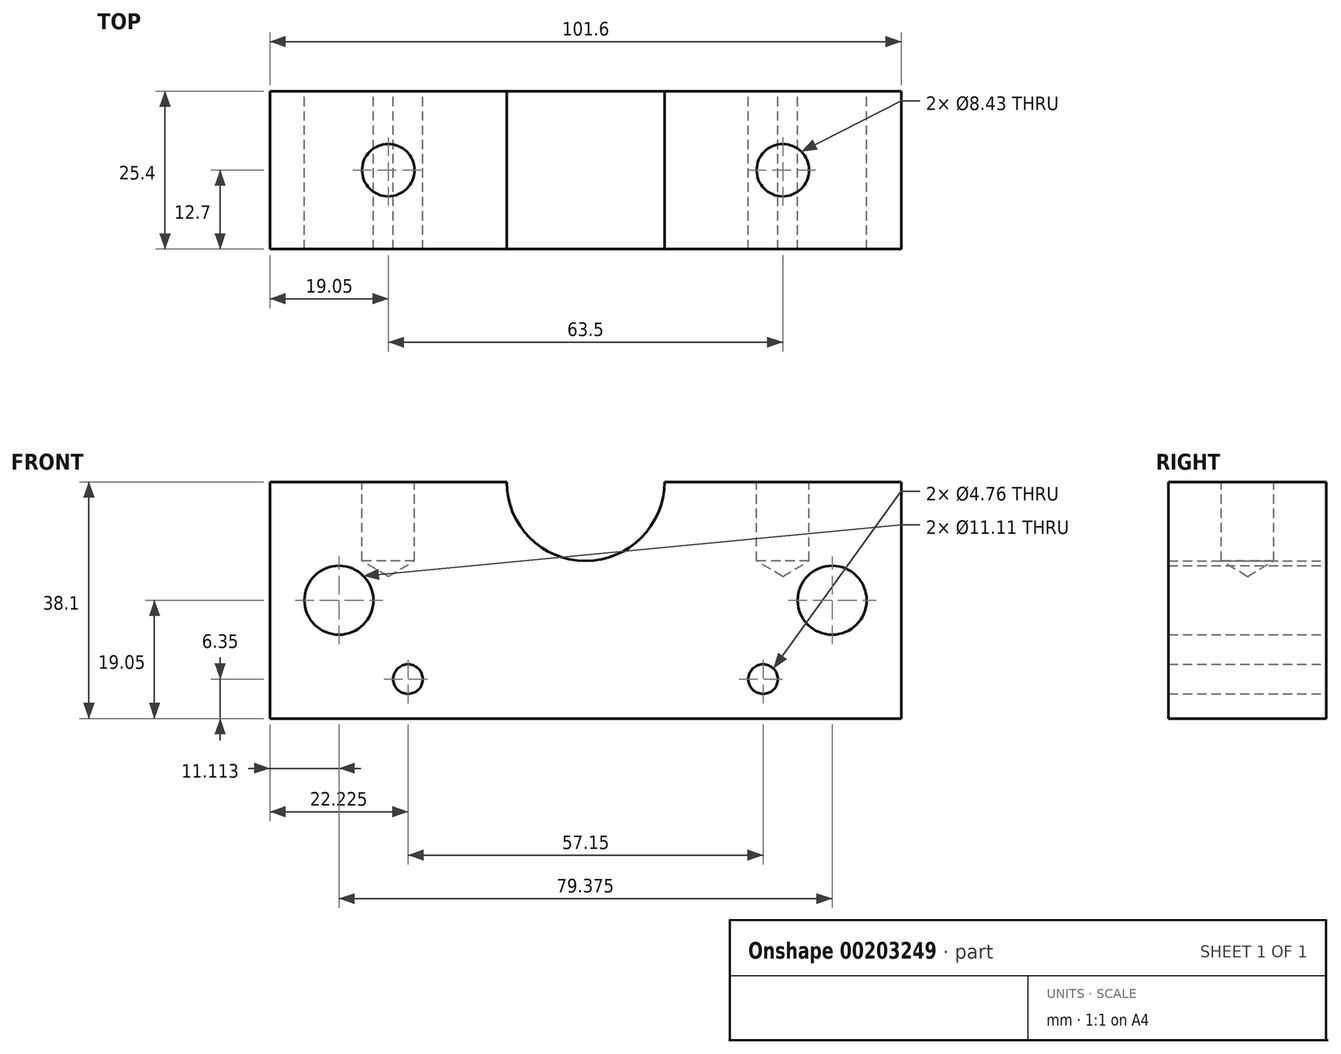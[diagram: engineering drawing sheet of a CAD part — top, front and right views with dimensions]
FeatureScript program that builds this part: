
annotation { "Feature Type Name" : "Feature", "Feature Type Description" : "" }
export const myFeature = defineFeature(function(context is Context, id is Id, definition is map)
    precondition{}
    {
        {
            var Q0;
            Q0=qCreatedBy(makeId("Front.planeOp"),FACE);
            var sketch = newSketch(context, id + "F0", { "sketchPlane" : qUnion([Q0])});
            skLineSegment(sketch, "E0.bottom", {"start": v(0, 0) * mm, "end": v(101.6, 0) * mm});
            skLineSegment(sketch, "E0.top", {"start": v(0, 38.1) * mm, "end": v(38.1, 38.1) * mm});
            skLineSegment(sketch, "E0.left", {"start": v(0, 0) * mm, "end": v(0, 38.1) * mm});
            skLineSegment(sketch, "E0.right", {"start": v(101.6, 0) * mm, "end": v(101.6, 38.1) * mm});
            skArc(sketch, "E1", {"start": v(38.1, 38.1) * mm, "mid": v(50.8, 25.4) * mm, "end": v(63.5, 38.1) * mm});
            skLineSegment(sketch, "E2.trimOffspring", {"start": v(63.5, 38.1) * mm, "end": v(101.6, 38.1) * mm});
            skCircle(sketch, "E3", {"center": v(11.11, 19.05) * mm, "radius": 5.56 * mm});
            skCircle(sketch, "E4", {"center": v(90.49, 19.05) * mm, "radius": 5.56 * mm});
            skCircle(sketch, "E5", {"center": v(79.38, 6.35) * mm, "radius": 2.38 * mm});
            skCircle(sketch, "E6", {"center": v(22.23, 6.35) * mm, "radius": 2.38 * mm});
            skSolve(sketch);
        }
        {
            var Q0;
            Q0 = qSketchRegion(id + "F0", true);
            extrude(context, id + "F1", {"entities" : qUnion([Q0]), "depth" : 25.4 * mm});
        }
        {
            var Q0;
            Q0=makeQuery(id+"F1.opExtrude","SWEPT_FACE",FACE,{"disambiguationData":[OSD([sQuery(id+"F0.wireOp",EDGE,"E0.top")])]});
            var sketch = newSketch(context, id + "F2", { "sketchPlane" : qUnion([Q0])});
            skPoint(sketch, "E7", {"position": v(19.05, -12.7) * mm});
            skPoint(sketch, "E8", {"position": v(82.55, -12.7) * mm});
            skSolve(sketch);
        }
        {
            var Q0;
            Q0=sQuery(id+"F2.wireOp",VERTEX,"E7");
            var Q1;
            Q1=sQuery(id+"F2.wireOp",VERTEX,"E8");
            var Q2;
            Q2=makeQuery(id+"F1.opExtrude","SWEPT_BODY",BODY,{"disambiguationData":[OSD([sQuery(id+"F0.wireOp",EDGE,"E0.bottom"),sQuery(id+"F0.wireOp",EDGE,"E0.top"),sQuery(id+"F0.wireOp",EDGE,"E0.left"),sQuery(id+"F0.wireOp",EDGE,"E0.right"),sQuery(id+"F0.wireOp",EDGE,"E1"),sQuery(id+"F0.wireOp",EDGE,"E2.trimOffspring"),sQuery(id+"F0.wireOp",EDGE,"E3"),sQuery(id+"F0.wireOp",EDGE,"E4"),sQuery(id+"F0.wireOp",EDGE,"E5"),sQuery(id+"F0.wireOp",EDGE,"E6")])]});
            hole(context, id + "F3", {"style" : HoleStyle.SIMPLE, "endStyle" : HoleEndStyle.BLIND, "standardTappedOrClearance" : lookupTablePath({ "standard" : "ANSI", "engagement" : "75%", "pitch" : "24 tpi", "size" : "3/8", "type" : "Tapped" }), "standardBlindInLast" : lookupTablePath({ "standard" : "ANSI", "engagement" : "75%", "pitch" : "24 tpi", "size" : "3/8", "type" : "Tapped" }), "holeDiameter" : 8.43 * mm, "holeDepth" : 12.7 * mm, "startFromSketch" : true, "locations" : qUnion([Q0, Q1]), "scope" : qUnion([Q2]), "majorDiameter" : 9.53 * mm});
        }
    });
